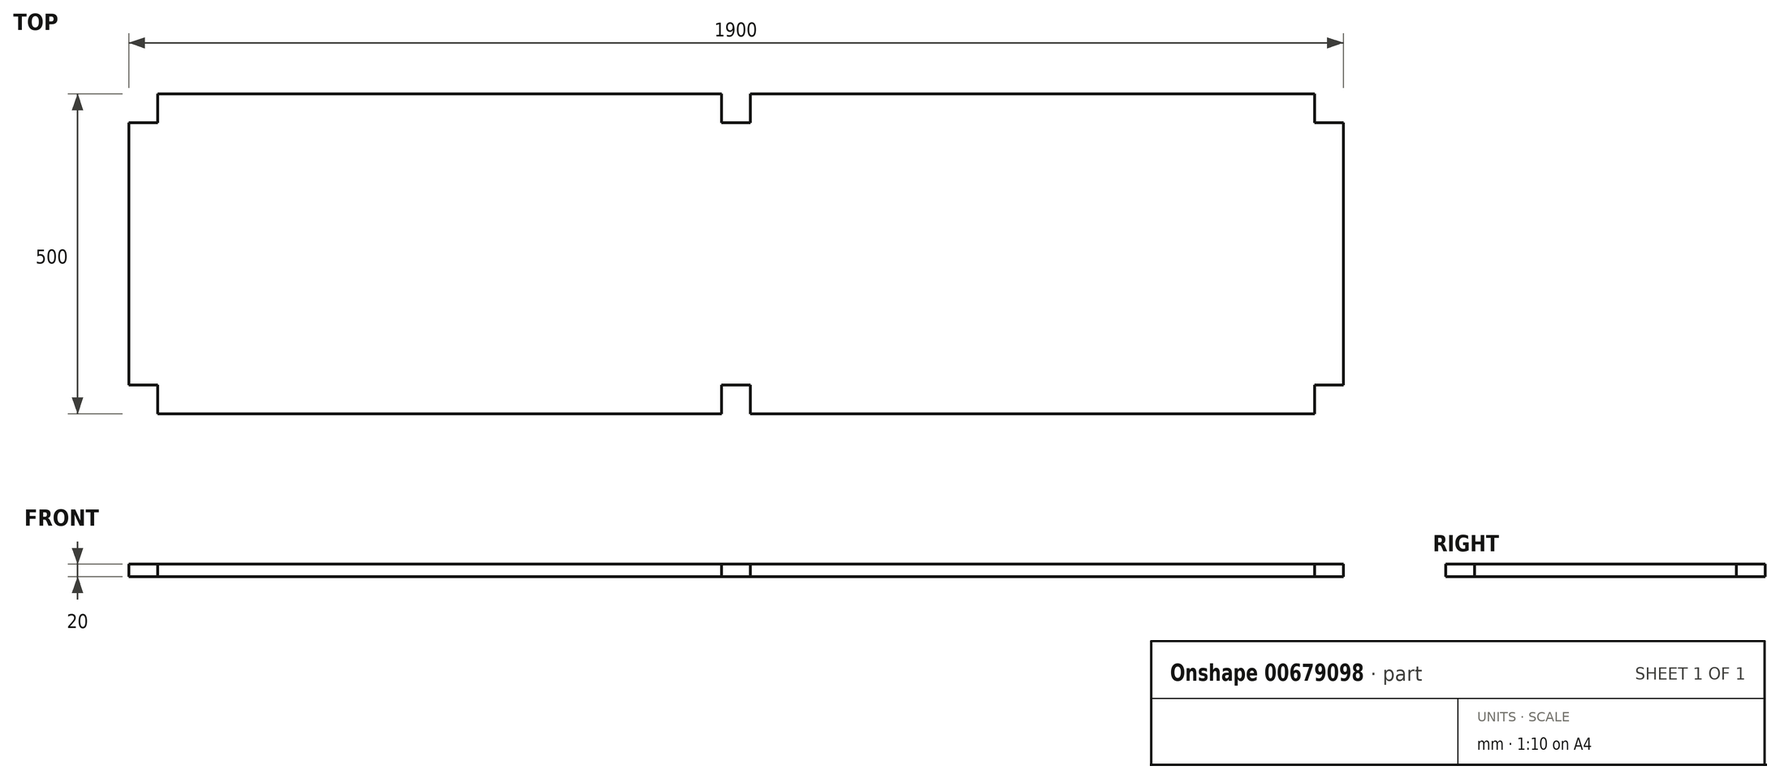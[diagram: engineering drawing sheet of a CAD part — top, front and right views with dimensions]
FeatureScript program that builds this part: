
annotation { "Feature Type Name" : "Feature", "Feature Type Description" : "" }
export const myFeature = defineFeature(function(context is Context, id is Id, definition is map)
    precondition{}
    {
        {
            var Q0;
            Q0=qCreatedBy(makeId("Top.planeOp"),FACE);
            var sketch = newSketch(context, id + "F0", { "sketchPlane" : qUnion([Q0])});
            skLineSegment(sketch, "E0.bottom", {"start": v(950, 250) * mm, "end": v(-950, 250) * mm});
            skLineSegment(sketch, "E0.top", {"start": v(950, -250) * mm, "end": v(-950, -250) * mm});
            skLineSegment(sketch, "E0.left", {"start": v(950, 250) * mm, "end": v(950, -250) * mm});
            skLineSegment(sketch, "E0.right", {"start": v(-950, 250) * mm, "end": v(-950, -250) * mm});
            skPoint(sketch, "E0.middle", {"position": v(0, 0) * mm});
            skSolve(sketch);
        }
        {
            var Q0;
            Q0 = qSketchRegion(id + "F0", true);
            extrude(context, id + "F1", {"entities" : qUnion([Q0]), "depth" : 20 * mm, "offsetDistance" : 25 * mm});
        }
        {
            var Q0;
            Q0=makeQuery(id+"F1.opExtrude","CAP_FACE",FACE,{"disambiguationData":[OSD([sQuery(id+"F0.wireOp",EDGE,"E0.bottom"),sQuery(id+"F0.wireOp",EDGE,"E0.top"),sQuery(id+"F0.wireOp",EDGE,"E0.left"),sQuery(id+"F0.wireOp",EDGE,"E0.right")])],"isStart":false});
            var sketch = newSketch(context, id + "F2", { "sketchPlane" : qUnion([Q0])});
            skLineSegment(sketch, "E1.bottom", {"start": v(-950, 250) * mm, "end": v(-905, 250) * mm});
            skLineSegment(sketch, "E1.top", {"start": v(-950, 205) * mm, "end": v(-905, 205) * mm});
            skLineSegment(sketch, "E1.left", {"start": v(-950, 250) * mm, "end": v(-950, 205) * mm});
            skLineSegment(sketch, "E1.right", {"start": v(-905, 250) * mm, "end": v(-905, 205) * mm});
            skLineSegment(sketch, "E2.bottom", {"start": v(-950, -250) * mm, "end": v(-905, -250) * mm});
            skLineSegment(sketch, "E2.top", {"start": v(-950, -205) * mm, "end": v(-905, -205) * mm});
            skLineSegment(sketch, "E2.left", {"start": v(-950, -250) * mm, "end": v(-950, -205) * mm});
            skLineSegment(sketch, "E2.right", {"start": v(-905, -250) * mm, "end": v(-905, -205) * mm});
            skLineSegment(sketch, "E3.bottom", {"start": v(950, 250) * mm, "end": v(905, 250) * mm});
            skLineSegment(sketch, "E3.top", {"start": v(950, 205) * mm, "end": v(905, 205) * mm});
            skLineSegment(sketch, "E3.left", {"start": v(950, 250) * mm, "end": v(950, 205) * mm});
            skLineSegment(sketch, "E3.right", {"start": v(905, 250) * mm, "end": v(905, 205) * mm});
            skLineSegment(sketch, "E4.bottom", {"start": v(950, -250) * mm, "end": v(905, -250) * mm});
            skLineSegment(sketch, "E4.top", {"start": v(950, -205) * mm, "end": v(905, -205) * mm});
            skLineSegment(sketch, "E4.left", {"start": v(950, -250) * mm, "end": v(950, -205) * mm});
            skLineSegment(sketch, "E4.right", {"start": v(905, -250) * mm, "end": v(905, -205) * mm});
            skLineSegment(sketch, "E5.bottom", {"start": v(22.5, 250) * mm, "end": v(-22.5, 250) * mm});
            skLineSegment(sketch, "E5.top", {"start": v(22.5, 205) * mm, "end": v(-22.5, 205) * mm});
            skLineSegment(sketch, "E5.left", {"start": v(22.5, 250) * mm, "end": v(22.5, 205) * mm});
            skLineSegment(sketch, "E5.right", {"start": v(-22.5, 250) * mm, "end": v(-22.5, 205) * mm});
            skPoint(sketch, "E5.middle", {"position": v(0, 227.5) * mm});
            skPoint(sketch, "E5.middle.positionSnap0", {"position": v(0, 250) * mm});
            skPoint(sketch, "E5.centerSnap0", {"position": v(0, 250) * mm});
            skLineSegment(sketch, "E6.bottom", {"start": v(22.5, -250) * mm, "end": v(-22.5, -250) * mm});
            skLineSegment(sketch, "E6.top", {"start": v(22.5, -205) * mm, "end": v(-22.5, -205) * mm});
            skLineSegment(sketch, "E6.left", {"start": v(22.5, -250) * mm, "end": v(22.5, -205) * mm});
            skLineSegment(sketch, "E6.right", {"start": v(-22.5, -250) * mm, "end": v(-22.5, -205) * mm});
            skPoint(sketch, "E6.middle", {"position": v(0, -227.5) * mm});
            skSolve(sketch);
        }
        {
            var Q0;
            Q0 = qSketchRegion(id + "F2", true);
            extrude(context, id + "F3", {"entities" : qUnion([Q0]), "operationType" : NewBodyOperationType.REMOVE, "endBound" : BoundingType.THROUGH_ALL, "oppositeDirection" : true, "depth" : 25 * mm, "offsetDistance" : 25 * mm});
        }
    });
